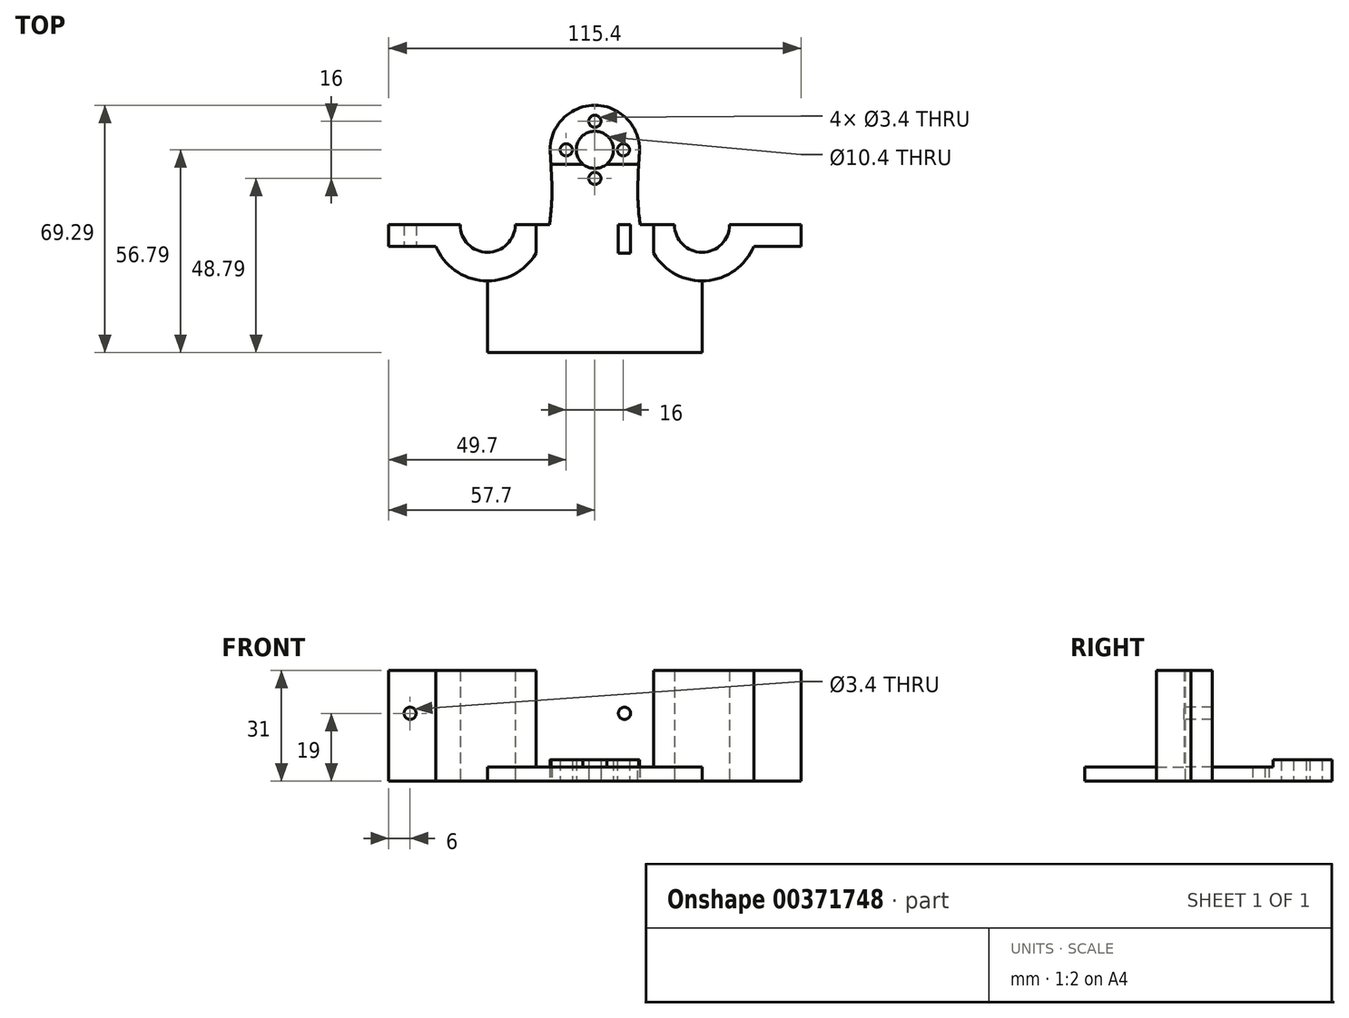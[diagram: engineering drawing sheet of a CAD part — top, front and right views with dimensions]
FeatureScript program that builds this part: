
annotation { "Feature Type Name" : "Feature", "Feature Type Description" : "" }
export const myFeature = defineFeature(function(context is Context, id is Id, definition is map)
    precondition{}
    {
        {
            var Q0;
            Q0=qCreatedBy(makeId("Top.planeOp"),FACE);
            var sketch = newSketch(context, id + "F0", { "sketchPlane" : qUnion([Q0])});
            skLineSegment(sketch, "E0", {"start": v(0, 0) * mm, "end": v(-22.3, 0) * mm});
            skLineSegment(sketch, "E1", {"start": v(0, 0) * mm, "end": v(22.3, 0) * mm});
            skArc(sketch, "E2", {"start": v(-37.7, 0) * mm, "mid": v(-30, -7.7) * mm, "end": v(-22.3, 0) * mm});
            skArc(sketch, "E3", {"start": v(22.3, 0) * mm, "mid": v(30, -7.7) * mm, "end": v(37.7, 0) * mm});
            skArc(sketch, "E4", {"start": v(-44.5, -6) * mm, "mid": v(-31.12, -15.66) * mm, "end": v(-16.5, -8) * mm});
            skArc(sketch, "E5", {"start": v(16.5, -8) * mm, "mid": v(31.12, -15.66) * mm, "end": v(44.5, -6) * mm});
            skLineSegment(sketch, "E6", {"start": v(-37.7, 0) * mm, "end": v(-45.7, 0) * mm});
            skLineSegment(sketch, "E7", {"start": v(37.7, 0) * mm, "end": v(45.7, 0) * mm});
            skLineSegment(sketch, "E8", {"start": v(-14.3, 0) * mm, "end": v(-14.3, -8) * mm, "construction": true});
            skLineSegment(sketch, "E9", {"start": v(-16.5, -8) * mm, "end": v(16.5, -8) * mm});
            skLineSegment(sketch, "E10", {"start": v(-30, -15.7) * mm, "end": v(-30, -35.79) * mm});
            skLineSegment(sketch, "E11", {"start": v(-30, -35.79) * mm, "end": v(30, -35.79) * mm});
            skPoint(sketch, "E11.endSnap0", {"position": v(30, -15.7) * mm});
            skLineSegment(sketch, "E12", {"start": v(30, -35.79) * mm, "end": v(30, -15.7) * mm});
            skLineSegment(sketch, "E13", {"start": v(0, 0) * mm, "end": v(0, 21) * mm, "construction": true});
            skCircle(sketch, "E14", {"center": v(0, 21) * mm, "radius": 5.2 * mm});
            skCircle(sketch, "E15", {"center": v(0, 21) * mm, "radius": 8 * mm, "construction": true});
            skArc(sketch, "E16", {"start": v(12.48, 20.24) * mm, "mid": v(0, 33.5) * mm, "end": v(-12.48, 20.24) * mm});
            skCircle(sketch, "E17", {"center": v(0, 29) * mm, "radius": 1.7 * mm});
            skCircle(sketch, "E18", {"center": v(8, 21) * mm, "radius": 1.7 * mm});
            skCircle(sketch, "E19", {"center": v(0, 13) * mm, "radius": 1.7 * mm});
            skCircle(sketch, "E20", {"center": v(-8, 21) * mm, "radius": 1.7 * mm});
            skFitSpline(sketch, "E21", {"points": [v(-12.69, 0) * mm, v(-12.02, 7.78) * mm, v(-12.48, 20.24) * mm], "startDerivative": vector(2, 16.58) * mm, "endDerivative": vector(-1.43, 23.63) * mm});
            skFitSpline(sketch, "E22.MirrorCS", {"points": [v(12.69, 0) * mm, v(12.02, 7.78) * mm, v(12.48, 20.24) * mm], "startDerivative": vector(-2, 16.58) * mm, "endDerivative": vector(1.43, 23.63) * mm});
            skLineSegment(sketch, "E23", {"start": v(-45.7, 0) * mm, "end": v(-57.7, 0) * mm});
            skLineSegment(sketch, "E24", {"start": v(-57.7, 0) * mm, "end": v(-57.7, -6) * mm});
            skLineSegment(sketch, "E25", {"start": v(-57.7, -6) * mm, "end": v(-44.5, -6) * mm});
            skLineSegment(sketch, "E26.MirrorCS", {"start": v(45.7, 0) * mm, "end": v(57.7, 0) * mm});
            skLineSegment(sketch, "E27.MirrorCS", {"start": v(57.7, 0) * mm, "end": v(57.7, -6) * mm});
            skLineSegment(sketch, "E28.MirrorCS", {"start": v(57.7, -6) * mm, "end": v(44.5, -6) * mm});
            skArc(sketch, "E29", {"start": v(-44.5, -6) * mm, "mid": v(-38.73, -13.05) * mm, "end": v(-30, -15.7) * mm});
            skSolve(sketch);
        }
        {
            var Q0;
            {var subQ8=sQuery(id+"F0.wireOp",EDGE,"E2");Q0=makeQuery(id+"F0.imprint","IMPRINT",FACE,{"disambiguationData":[TD([[makeQuery(id+"F0.imprint","IMPRINT",EDGE,{"derivedFrom":subQ8}),-1.0]])]});}
            extrude(context, id + "F1", {"entities" : qUnion([Q0]), "depth" : 31 * mm});
        }
        {
            var Q0;
            Q0=makeQuery(id+"F0.imprint","IMPRINT",FACE,{"disambiguationData":[TD([[makeQuery(id+"F0.imprint","IMPRINT",EDGE,{"derivedFrom":sQuery(id+"F0.wireOp",EDGE,"E14")}),-1.0]])]});
            extrude(context, id + "F2", {"entities" : qUnion([Q0]), "operationType" : NewBodyOperationType.ADD, "depth" : 6 * mm});
        }
        {
            var Q0;
            {var subQ1=sQuery(id+"F0.wireOp",EDGE,"E9");Q0=makeQuery(id+"F0.imprint","IMPRINT",FACE,{"disambiguationData":[TD([[makeQuery(id+"F0.imprint","IMPRINT",EDGE,{"derivedFrom":subQ1}),-1.0]])]});}
            extrude(context, id + "F3", {"entities" : qUnion([Q0]), "operationType" : NewBodyOperationType.ADD, "depth" : 4 * mm});
        }
        {
            var Q0;
            Q0=makeQuery(id+"F1.opExtrude","SWEPT_FACE",FACE,{"disambiguationData":[OSD([sQuery(id+"F0.wireOp",EDGE,"E9")])]});
            var sketch = newSketch(context, id + "F4", { "sketchPlane" : qUnion([Q0])});
            skLineSegment(sketch, "E30", {"start": v(0, 0) * mm, "end": v(0, 19) * mm, "construction": true});
            skPoint(sketch, "E30.endSnap0", {"position": v(0, 4) * mm});
            skLineSegment(sketch, "E31", {"start": v(0, 19) * mm, "end": v(-30, 19) * mm, "construction": true});
            skLineSegment(sketch, "E32", {"start": v(-30, 19) * mm, "end": v(-8.3, 19) * mm, "construction": true});
            skLineSegment(sketch, "E33", {"start": v(-30, 19) * mm, "end": v(-51.7, 19) * mm, "construction": true});
            skCircle(sketch, "E34", {"center": v(-51.7, 19) * mm, "radius": 1.7 * mm});
            skCircle(sketch, "E35", {"center": v(-8.3, 19) * mm, "radius": 1.7 * mm});
            skCircle(sketch, "E36.MirrorC", {"center": v(8.3, 19) * mm, "radius": 1.7 * mm});
            skCircle(sketch, "E37.MirrorC", {"center": v(51.7, 19) * mm, "radius": 1.7 * mm});
            skSolve(sketch);
        }
        {
            var Q0;
            Q0=makeQuery(id+"F4.imprint","IMPRINT",FACE,{"disambiguationData":[TD([[makeQuery(id+"F4.imprint","IMPRINT",EDGE,{"derivedFrom":sQuery(id+"F4.wireOp",EDGE,"E34")}),1.0]])]});
            var Q1;
            Q1=makeQuery(id+"F4.imprint","IMPRINT",FACE,{"disambiguationData":[TD([[makeQuery(id+"F4.imprint","IMPRINT",EDGE,{"derivedFrom":sQuery(id+"F4.wireOp",EDGE,"E35")}),1.0]])]});
            var Q2;
            Q2=makeQuery(id+"F4.imprint","IMPRINT",FACE,{"disambiguationData":[TD([[makeQuery(id+"F4.imprint","IMPRINT",EDGE,{"derivedFrom":sQuery(id+"F4.wireOp",EDGE,"E36.MirrorC")}),-1.0]])]});
            var Q3;
            Q3=makeQuery(id+"F4.imprint","IMPRINT",FACE,{"disambiguationData":[TD([[makeQuery(id+"F4.imprint","IMPRINT",EDGE,{"derivedFrom":sQuery(id+"F4.wireOp",EDGE,"E37.MirrorC")}),-1.0]])]});
            extrude(context, id + "F5", {"entities" : qUnion([Q0, Q1, Q2, Q3]), "operationType" : NewBodyOperationType.REMOVE, "oppositeDirection" : true, "depth" : 25 * mm});
        }
    });
